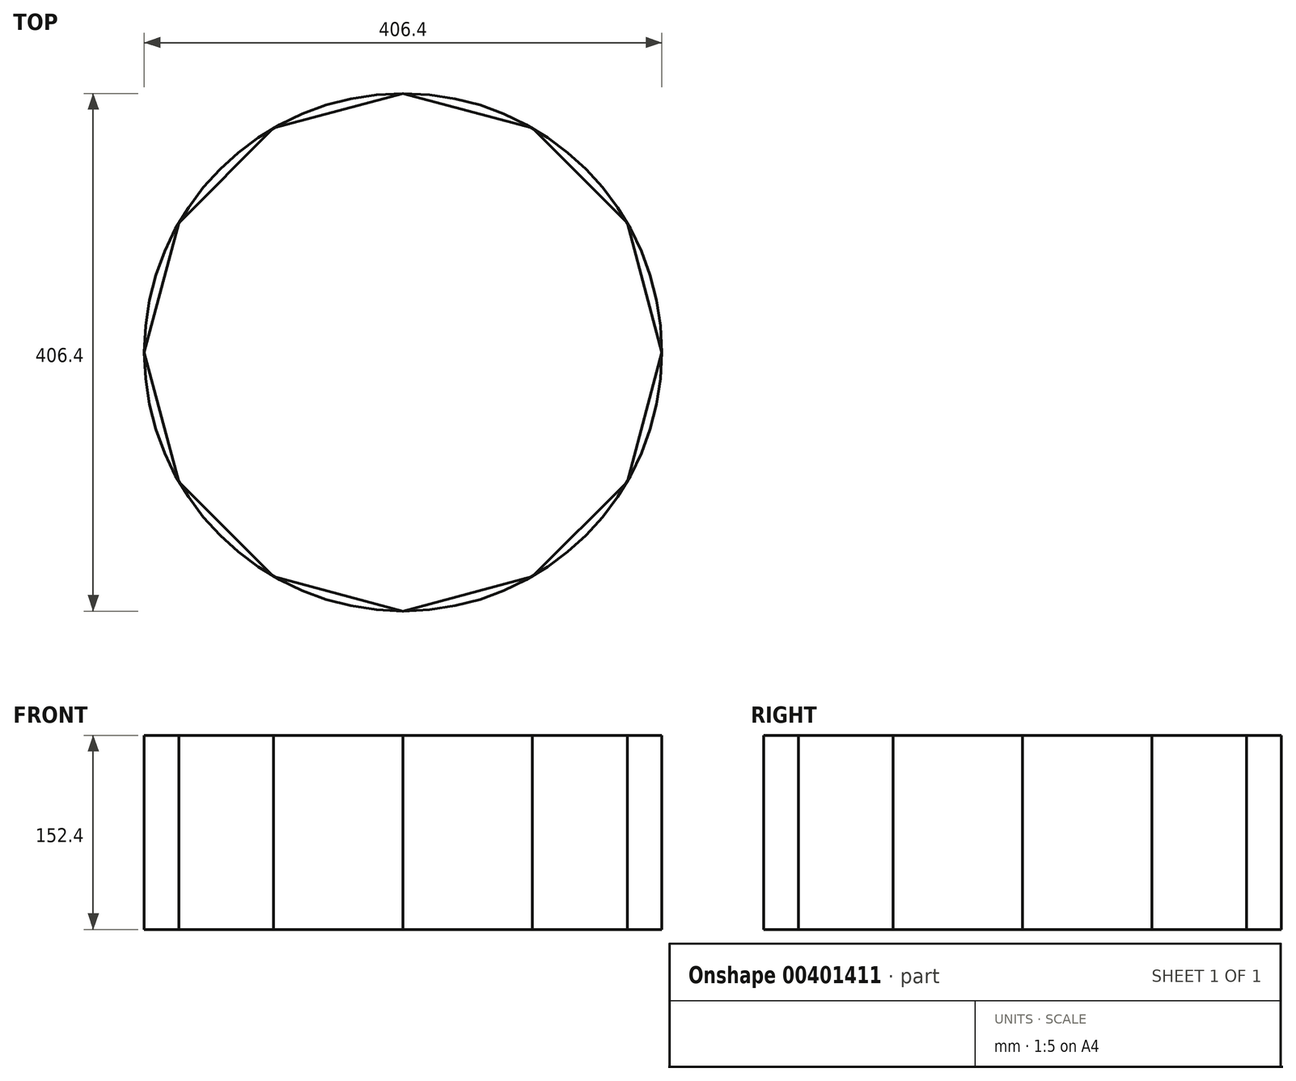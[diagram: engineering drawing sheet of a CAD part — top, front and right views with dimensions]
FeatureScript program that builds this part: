
annotation { "Feature Type Name" : "Feature", "Feature Type Description" : "" }
export const myFeature = defineFeature(function(context is Context, id is Id, definition is map)
    precondition{}
    {
        {
            var Q0;
            Q0=qCreatedBy(makeId("Top.planeOp"),FACE);
            var sketch = newSketch(context, id + "F0", { "sketchPlane" : qUnion([Q0])});
            skCircle(sketch, "E0", {"center": v(0, 0) * mm, "radius": 203.2 * mm});
            skSolve(sketch);
        }
        {
            var Q0;
            Q0=makeQuery(id+"F0.imprint","IMPRINT",FACE,{"disambiguationData":[TD([[makeQuery(id+"F0.imprint","IMPRINT",EDGE,{"derivedFrom":sQuery(id+"F0.wireOp",EDGE,"E0")}),1.0]])]});
            var sketch = newSketch(context, id + "F1", { "sketchPlane" : qUnion([Q0])});
            skSolve(sketch);
        }
        {
            var Q0;
            Q0=makeQuery(id+"F1.imprint","IMPRINT",FACE,{"disambiguationData":[TD([[makeQuery(id+"F1.imprint","IMPRINT",EDGE,{"derivedFrom":makeQuery(id+"F0.imprint","IMPRINT",EDGE,{"derivedFrom":sQuery(id+"F0.wireOp",EDGE,"E0")})}),1.0]])]});
            var sketch = newSketch(context, id + "F2", { "sketchPlane" : qUnion([Q0])});
            skSolve(sketch);
        }
        {
            var Q0;
            Q0=makeQuery(id+"F1.imprint","IMPRINT",FACE,{"disambiguationData":[TD([[makeQuery(id+"F1.imprint","IMPRINT",EDGE,{"derivedFrom":makeQuery(id+"F0.imprint","IMPRINT",EDGE,{"derivedFrom":sQuery(id+"F0.wireOp",EDGE,"E0")})}),1.0]])]});
            var sketch = newSketch(context, id + "F3", { "sketchPlane" : qUnion([Q0])});
            skSolve(sketch);
        }
        {
            var Q0;
            Q0=makeQuery(id+"F3.imprint","IMPRINT",FACE,{"disambiguationData":[TD([[makeQuery(id+"F3.imprint","IMPRINT",EDGE,{"derivedFrom":makeQuery(id+"F1.imprint","IMPRINT",EDGE,{"derivedFrom":makeQuery(id+"F0.imprint","IMPRINT",EDGE,{"derivedFrom":sQuery(id+"F0.wireOp",EDGE,"E0")})})}),1.0]])]});
            var sketch = newSketch(context, id + "F4", { "sketchPlane" : qUnion([Q0])});
            skSolve(sketch);
        }
        {
            var Q0;
            Q0=makeQuery(id+"F4.imprint","IMPRINT",FACE,{"disambiguationData":[TD([[makeQuery(id+"F4.imprint","IMPRINT",EDGE,{"derivedFrom":makeQuery(id+"F3.imprint","IMPRINT",EDGE,{"derivedFrom":makeQuery(id+"F1.imprint","IMPRINT",EDGE,{"derivedFrom":makeQuery(id+"F0.imprint","IMPRINT",EDGE,{"derivedFrom":sQuery(id+"F0.wireOp",EDGE,"E0")})})})}),1.0]])]});
            var sketch = newSketch(context, id + "F5", { "sketchPlane" : qUnion([Q0])});
            skCircle(sketch, "E1.cCircle", {"center": v(0, 0) * mm, "radius": 203.2 * mm, "construction": true});
            skLineSegment(sketch, "E1.0", {"start": v(203.2, 0) * mm, "end": v(175.98, -101.6) * mm});
            skLineSegment(sketch, "E1.1", {"start": v(175.98, -101.6) * mm, "end": v(101.6, -175.98) * mm});
            skLineSegment(sketch, "E1.2", {"start": v(101.6, -175.98) * mm, "end": v(0, -203.2) * mm});
            skLineSegment(sketch, "E1.3", {"start": v(0, -203.2) * mm, "end": v(-101.6, -175.98) * mm});
            skLineSegment(sketch, "E1.4", {"start": v(-101.6, -175.98) * mm, "end": v(-175.98, -101.6) * mm});
            skLineSegment(sketch, "E1.5", {"start": v(-175.98, -101.6) * mm, "end": v(-203.2, 0) * mm});
            skLineSegment(sketch, "E1.6", {"start": v(-203.2, 0) * mm, "end": v(-175.98, 101.6) * mm});
            skLineSegment(sketch, "E1.7", {"start": v(-175.98, 101.6) * mm, "end": v(-101.6, 175.98) * mm});
            skLineSegment(sketch, "E1.8", {"start": v(-101.6, 175.98) * mm, "end": v(0, 203.2) * mm});
            skLineSegment(sketch, "E1.9", {"start": v(0, 203.2) * mm, "end": v(101.6, 175.98) * mm});
            skLineSegment(sketch, "E1.10", {"start": v(101.6, 175.98) * mm, "end": v(175.98, 101.6) * mm});
            skLineSegment(sketch, "E1.11", {"start": v(175.98, 101.6) * mm, "end": v(203.2, 0) * mm});
            skSolve(sketch);
        }
        {
            var Q0;
            Q0=makeQuery(id+"F5.imprint","IMPRINT",FACE,{"disambiguationData":[TD([[makeQuery(id+"F5.imprint","IMPRINT",EDGE,{"derivedFrom":sQuery(id+"F5.wireOp",EDGE,"E1.0")}),-1.0]])]});
            var Q1;
            Q1=makeQuery(id+"F1.imprint","IMPRINT",FACE,{"disambiguationData":[TD([[makeQuery(id+"F1.imprint","IMPRINT",EDGE,{"derivedFrom":makeQuery(id+"F0.imprint","IMPRINT",EDGE,{"derivedFrom":sQuery(id+"F0.wireOp",EDGE,"E0")})}),1.0]])]});
            extrude(context, id + "F6", {"entities" : qUnion([Q0, Q1]), "depth" : 152.4 * mm, "offsetDistance" : 25.4 * mm});
        }
    });
